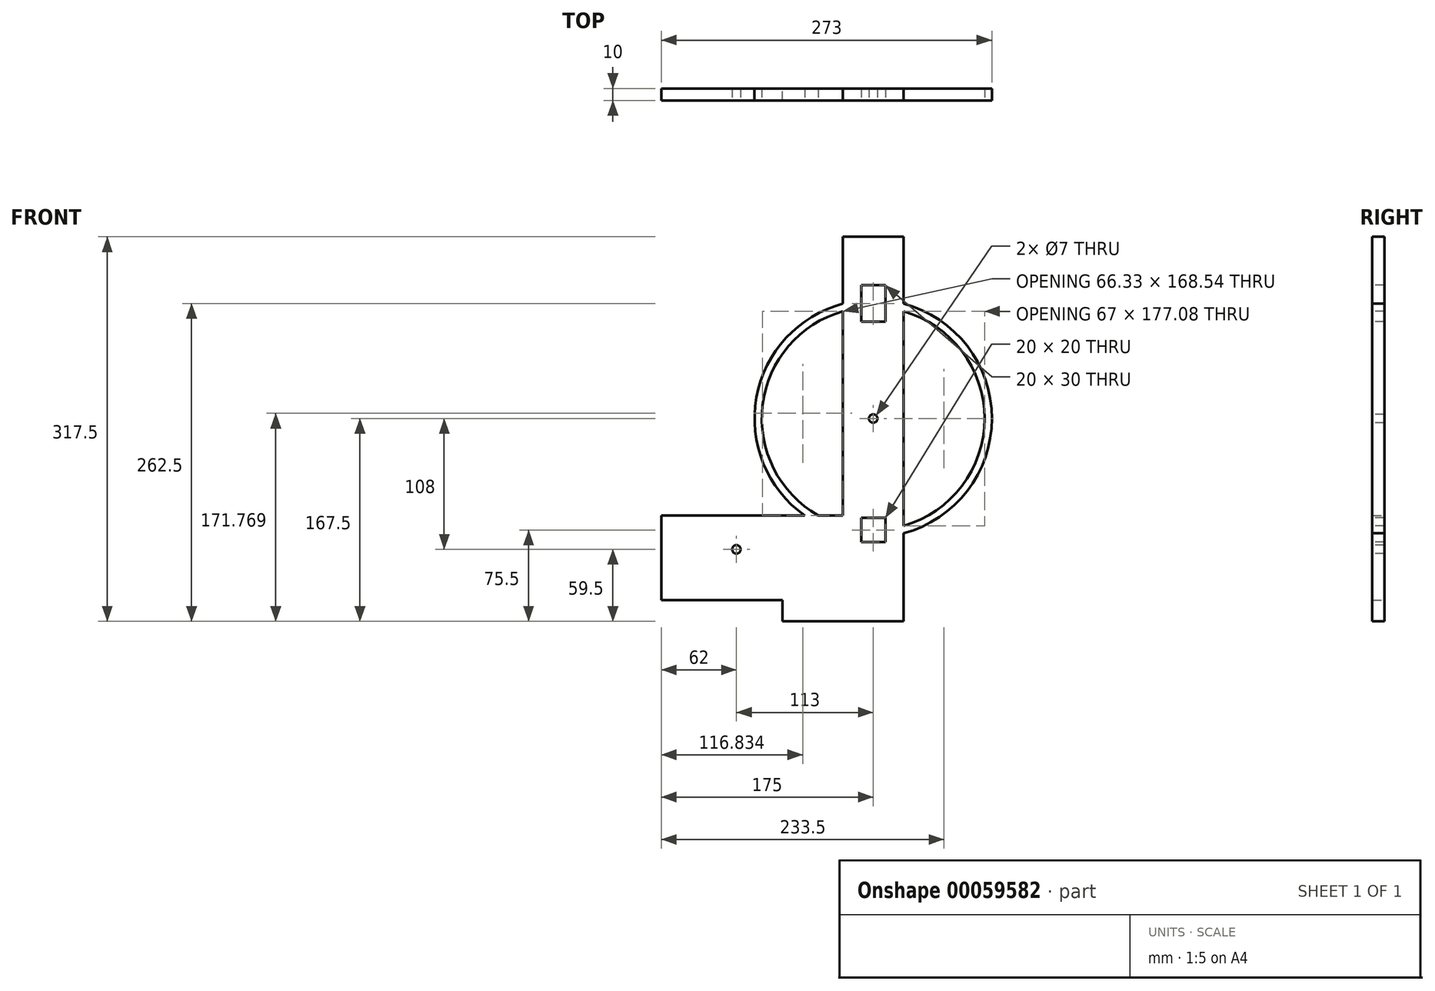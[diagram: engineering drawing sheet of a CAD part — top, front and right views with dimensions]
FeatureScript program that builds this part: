
annotation { "Feature Type Name" : "Feature", "Feature Type Description" : "" }
export const myFeature = defineFeature(function(context is Context, id is Id, definition is map)
    precondition{}
    {
        {
            var Q0;
            Q0=qCreatedBy(makeId("Front.planeOp"),FACE);
            var sketch = newSketch(context, id + "F0", { "sketchPlane" : qUnion([Q0])});
            skLineSegment(sketch, "E0.bottom", {"start": v(-25, 150) * mm, "end": v(25, 150) * mm});
            skLineSegment(sketch, "E0.left", {"start": v(-25, 150) * mm, "end": v(-25, -80) * mm});
            skLineSegment(sketch, "E0.right", {"start": v(25, 150) * mm, "end": v(25, -150) * mm});
            skLineSegment(sketch, "E1.top", {"start": v(-25, -80) * mm, "end": v(-175, -80) * mm});
            skLineSegment(sketch, "E1.right", {"start": v(-175, -150) * mm, "end": v(-175, -80) * mm});
            skLineSegment(sketch, "E2", {"start": v(-175, -150) * mm, "end": v(25, -150) * mm});
            skSolve(sketch);
        }
        {
            var Q0;
            Q0 = qSketchRegion(id + "F0", true);
            extrude(context, id + "F1", {"entities" : qUnion([Q0]), "depth" : 10 * mm});
        }
        {
            var Q0;
            Q0=makeQuery(id+"F1.opExtrude","CAP_FACE",FACE,{"disambiguationData":[OSD([sQuery(id+"F0.wireOp",EDGE,"E0.bottom"),sQuery(id+"F0.wireOp",EDGE,"E0.top"),sQuery(id+"F0.wireOp",EDGE,"E0.left"),sQuery(id+"F0.wireOp",EDGE,"E0.right"),sQuery(id+"F0.wireOp",EDGE,"E1.bottom"),sQuery(id+"F0.wireOp",EDGE,"E1.top"),sQuery(id+"F0.wireOp",EDGE,"E1.right")])],"isStart":false});
            var sketch = newSketch(context, id + "F2", { "sketchPlane" : qUnion([Q0])});
            skCircle(sketch, "E3", {"center": v(0, 0) * mm, "radius": 95 * mm, "construction": true});
            skCircle(sketch, "E4", {"center": v(0, 0) * mm, "radius": 98 * mm});
            skCircle(sketch, "E5", {"center": v(0, 0) * mm, "radius": 92 * mm});
            skSolve(sketch);
        }
        {
            var Q0;
            Q0 = qSketchRegion(id + "F2", true);
            extrude(context, id + "F3", {"entities" : qUnion([Q0]), "operationType" : NewBodyOperationType.ADD, "oppositeDirection" : true, "depth" : 10 * mm});
        }
        {
            var Q0;
            Q0=makeQuery(id+"F1.opExtrude","SWEPT_FACE",FACE,{"disambiguationData":[OSD([sQuery(id+"F0.wireOp",EDGE,"E2")])]});
            var sketch = newSketch(context, id + "F4", { "sketchPlane" : qUnion([Q0])});
            skLineSegment(sketch, "E6.bottom", {"start": v(25, 10) * mm, "end": v(-75, 10) * mm});
            skLineSegment(sketch, "E6.top", {"start": v(25, 0) * mm, "end": v(-75, 0) * mm});
            skLineSegment(sketch, "E6.left", {"start": v(25, 10) * mm, "end": v(25, 0) * mm});
            skLineSegment(sketch, "E6.right", {"start": v(-75, 10) * mm, "end": v(-75, 0) * mm});
            skSolve(sketch);
        }
        {
            var Q0;
            Q0 = qSketchRegion(id + "F4", true);
            extrude(context, id + "F5", {"entities" : qUnion([Q0]), "operationType" : NewBodyOperationType.ADD, "depth" : 17.5 * mm});
        }
        {
            var Q0;
            Q0=makeQuery(id+"F5.boolean.opBoolean","MERGE",FACE,{"derivedFrom":[makeQuery(id+"F3.boolean.opBoolean","MERGE",FACE,{"derivedFrom":[makeQuery(id+"F1.opExtrude","CAP_FACE",FACE,{"disambiguationData":[OSD([sQuery(id+"F0.wireOp",EDGE,"E0.bottom"),sQuery(id+"F0.wireOp",EDGE,"E0.top"),sQuery(id+"F0.wireOp",EDGE,"E0.left"),sQuery(id+"F0.wireOp",EDGE,"E0.right"),sQuery(id+"F0.wireOp",EDGE,"E1.bottom"),sQuery(id+"F0.wireOp",EDGE,"E1.top"),sQuery(id+"F0.wireOp",EDGE,"E1.right")])],"isStart":false}),makeQuery(id+"F3.opExtrude","CAP_FACE",FACE,{"disambiguationData":[OSD([sQuery(id+"F2.wireOp",EDGE,"E4"),sQuery(id+"F2.wireOp",EDGE,"E5")])],"isStart":true})]}),makeQuery(id+"F5.opExtrude","SWEPT_FACE",FACE,{"disambiguationData":[OSD([sQuery(id+"F4.wireOp",EDGE,"BhvBbVAg-w6V3-QJHI-VM8m-rcusInK2M3kt.bottom")])]})]});
            var sketch = newSketch(context, id + "F6", { "sketchPlane" : qUnion([Q0])});
            skLineSegment(sketch, "E7", {"start": v(0, 0) * mm, "end": v(0, -95) * mm, "construction": true});
            skLineSegment(sketch, "E8.bottom", {"start": v(-10, -82) * mm, "end": v(10, -82) * mm});
            skLineSegment(sketch, "E8.top", {"start": v(-10, -102) * mm, "end": v(10, -102) * mm});
            skLineSegment(sketch, "E8.left", {"start": v(-10, -82) * mm, "end": v(-10, -102) * mm});
            skLineSegment(sketch, "E8.right", {"start": v(10, -82) * mm, "end": v(10, -102) * mm});
            skPoint(sketch, "E8.middle", {"position": v(0, -92) * mm});
            skLineSegment(sketch, "E9", {"start": v(0, 0) * mm, "end": v(0, 95) * mm, "construction": true});
            skLineSegment(sketch, "E10.bottom", {"start": v(-10, 110) * mm, "end": v(10, 110) * mm});
            skLineSegment(sketch, "E10.top", {"start": v(-10, 80) * mm, "end": v(10, 80) * mm});
            skLineSegment(sketch, "E10.left", {"start": v(-10, 110) * mm, "end": v(-10, 80) * mm});
            skLineSegment(sketch, "E10.right", {"start": v(10, 110) * mm, "end": v(10, 80) * mm});
            skPoint(sketch, "E10.middle", {"position": v(0, 95) * mm});
            skCircle(sketch, "E11", {"center": v(0, 0) * mm, "radius": 3.5 * mm});
            skCircle(sketch, "E12", {"center": v(-113, -108) * mm, "radius": 3.5 * mm});
            skSolve(sketch);
        }
        {
            var Q0;
            Q0 = qSketchRegion(id + "F6", true);
            extrude(context, id + "F7", {"entities" : qUnion([Q0]), "operationType" : NewBodyOperationType.REMOVE, "oppositeDirection" : true, "depth" : 10 * mm});
        }
    });
